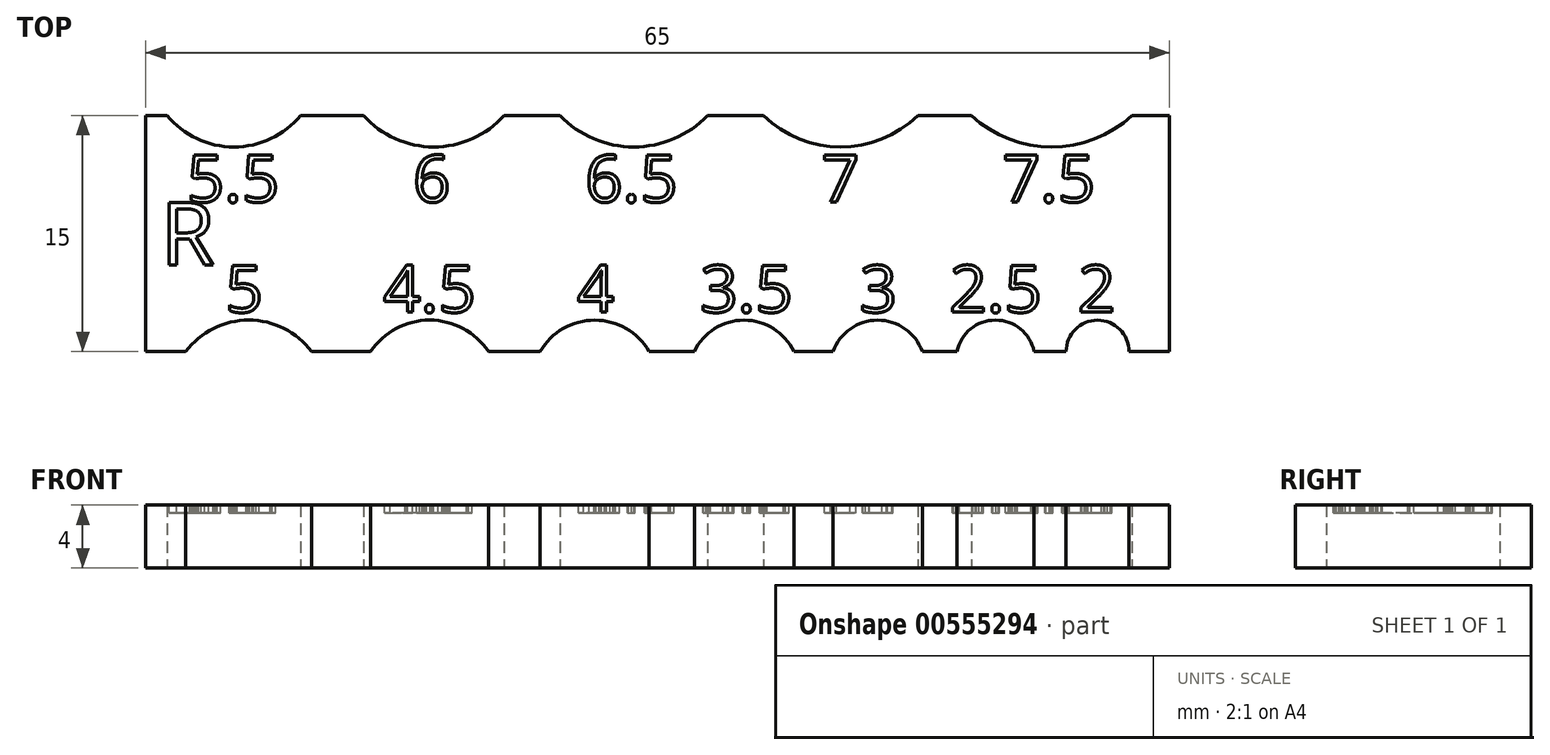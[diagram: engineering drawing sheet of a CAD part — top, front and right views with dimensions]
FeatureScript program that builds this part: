
annotation { "Feature Type Name" : "Feature", "Feature Type Description" : "" }
export const myFeature = defineFeature(function(context is Context, id is Id, definition is map)
    precondition{}
    {
        {
            var Q0;
            Q0=qCreatedBy(makeId("Top.planeOp"),FACE);
            var sketch = newSketch(context, id + "F0", { "sketchPlane" : qUnion([Q0])});
            skLineSegment(sketch, "E0", {"start": v(-84.54, 17.53) * mm, "end": v(-82, 17.53) * mm});
            skLineSegment(sketch, "E1", {"start": v(-95.27, 19.53) * mm, "end": v(54.73, 19.53) * mm, "construction": true});
            skArc(sketch, "E2", {"start": v(-74, 17.53) * mm, "mid": v(-78, 19.53) * mm, "end": v(-82, 17.53) * mm});
            skPoint(sketch, "E2.first.point", {"position": v(-74, 17.53) * mm});
            skPoint(sketch, "E2.second.point", {"position": v(-74, 17.53) * mm});
            skPoint(sketch, "E2.third.point", {"position": v(-78, 19.53) * mm});
            skArc(sketch, "E3.1.0.0", {"start": v(-62.77, 17.53) * mm, "mid": v(-66.52, 19.53) * mm, "end": v(-70.26, 17.53) * mm});
            skArc(sketch, "E3.2.0.0", {"start": v(-52.56, 17.53) * mm, "mid": v(-56.03, 19.53) * mm, "end": v(-59.5, 17.53) * mm});
            skArc(sketch, "E4.1.0.0", {"start": v(-43.38, 17.53) * mm, "mid": v(-46.54, 19.53) * mm, "end": v(-49.7, 17.53) * mm});
            skArc(sketch, "E4.2.0.0", {"start": v(-35.23, 17.53) * mm, "mid": v(-38.06, 19.53) * mm, "end": v(-40.88, 17.53) * mm});
            skArc(sketch, "E4.3.0.0", {"start": v(-28.12, 17.53) * mm, "mid": v(-30.57, 19.53) * mm, "end": v(-33.02, 17.53) * mm});
            skArc(sketch, "E4.4.0.0", {"start": v(-22.1, 17.53) * mm, "mid": v(-24.1, 19.53) * mm, "end": v(-26.1, 17.53) * mm});
            skLineSegment(sketch, "E5.trimOffspring", {"start": v(-22.1, 17.53) * mm, "end": v(-19.54, 17.53) * mm});
            skLineSegment(sketch, "E6.trimOffspring", {"start": v(-28.12, 17.53) * mm, "end": v(-26.1, 17.53) * mm});
            skLineSegment(sketch, "E7.trimOffspring", {"start": v(-35.23, 17.53) * mm, "end": v(-33.02, 17.53) * mm});
            skLineSegment(sketch, "E8.trimOffspring", {"start": v(-43.38, 17.53) * mm, "end": v(-40.88, 17.53) * mm});
            skLineSegment(sketch, "E9.trimOffspring", {"start": v(-52.56, 17.53) * mm, "end": v(-49.7, 17.53) * mm});
            skLineSegment(sketch, "E10.trimOffspring", {"start": v(-62.77, 17.53) * mm, "end": v(-59.5, 17.53) * mm});
            skLineSegment(sketch, "E11.trimOffspring", {"start": v(-74, 17.53) * mm, "end": v(-70.26, 17.53) * mm});
            skLineSegment(sketch, "E12", {"start": v(-84.54, 17.53) * mm, "end": v(-84.54, 32.53) * mm});
            skLineSegment(sketch, "E13", {"start": v(-84.54, 32.53) * mm, "end": v(-83.2, 32.53) * mm});
            skLineSegment(sketch, "E14", {"start": v(-19.54, 32.53) * mm, "end": v(-19.54, 17.53) * mm});
            skLineSegment(sketch, "E15", {"start": v(-84.54, 30.53) * mm, "end": v(-14.52, 30.53) * mm, "construction": true});
            skArc(sketch, "E16", {"start": v(-83.2, 32.53) * mm, "mid": v(-78.95, 30.53) * mm, "end": v(-74.7, 32.53) * mm});
            skPoint(sketch, "E16.first.point", {"position": v(-78.95, 30.53) * mm});
            skPoint(sketch, "E16.second.point", {"position": v(-74.7, 32.53) * mm});
            skPoint(sketch, "E16.third.point", {"position": v(-83.2, 32.53) * mm});
            skArc(sketch, "E17.1.0.0", {"start": v(-70.72, 32.53) * mm, "mid": v(-66.25, 30.53) * mm, "end": v(-61.78, 32.53) * mm});
            skArc(sketch, "E17.2.0.0", {"start": v(-58.24, 32.53) * mm, "mid": v(-53.55, 30.53) * mm, "end": v(-48.86, 32.53) * mm});
            skArc(sketch, "E17.3.0.0", {"start": v(-45.3, 32.53) * mm, "mid": v(-40.41, 30.53) * mm, "end": v(-35.51, 32.53) * mm});
            skArc(sketch, "E17.4.0.0", {"start": v(-32.1, 32.53) * mm, "mid": v(-27, 30.53) * mm, "end": v(-21.9, 32.53) * mm});
            skLineSegment(sketch, "E18.trimOffspring", {"start": v(-74.7, 32.53) * mm, "end": v(-70.72, 32.53) * mm});
            skLineSegment(sketch, "E19.trimOffspring", {"start": v(-61.78, 32.53) * mm, "end": v(-58.24, 32.53) * mm});
            skLineSegment(sketch, "E20.trimOffspring", {"start": v(-48.86, 32.53) * mm, "end": v(-45.3, 32.53) * mm});
            skLineSegment(sketch, "E21.trimOffspring", {"start": v(-35.51, 32.53) * mm, "end": v(-32.1, 32.53) * mm});
            skLineSegment(sketch, "E22.trimOffspring", {"start": v(-21.9, 32.53) * mm, "end": v(-19.54, 32.53) * mm});
            skSolve(sketch);
        }
        {
            var Q0;
            Q0 = qSketchRegion(id + "F0", true);
            extrude(context, id + "F1", {"entities" : qUnion([Q0]), "depth" : 4 * mm, "offsetDistance" : 25 * mm});
        }
        {
            var Q0;
            Q0=makeQuery(id+"F1.opExtrude","CAP_FACE",FACE,{"disambiguationData":[OSD([sQuery(id+"F0.wireOp",EDGE,"E0"),sQuery(id+"F0.wireOp",EDGE,"E2"),sQuery(id+"F0.wireOp",EDGE,"E3.1.0.0"),sQuery(id+"F0.wireOp",EDGE,"E3.2.0.0"),sQuery(id+"F0.wireOp",EDGE,"E4.1.0.0"),sQuery(id+"F0.wireOp",EDGE,"E4.2.0.0"),sQuery(id+"F0.wireOp",EDGE,"E4.3.0.0"),sQuery(id+"F0.wireOp",EDGE,"E4.4.0.0"),sQuery(id+"F0.wireOp",EDGE,"E5.trimOffspring"),sQuery(id+"F0.wireOp",EDGE,"E6.trimOffspring"),sQuery(id+"F0.wireOp",EDGE,"E7.trimOffspring"),sQuery(id+"F0.wireOp",EDGE,"E8.trimOffspring"),sQuery(id+"F0.wireOp",EDGE,"E9.trimOffspring"),sQuery(id+"F0.wireOp",EDGE,"E10.trimOffspring"),sQuery(id+"F0.wireOp",EDGE,"E11.trimOffspring"),sQuery(id+"F0.wireOp",EDGE,"E12"),sQuery(id+"F0.wireOp",EDGE,"E13"),sQuery(id+"F0.wireOp",EDGE,"E14"),sQuery(id+"F0.wireOp",EDGE,"E16"),sQuery(id+"F0.wireOp",EDGE,"E17.1.0.0"),sQuery(id+"F0.wireOp",EDGE,"E17.2.0.0"),sQuery(id+"F0.wireOp",EDGE,"E17.3.0.0"),sQuery(id+"F0.wireOp",EDGE,"E17.4.0.0"),sQuery(id+"F0.wireOp",EDGE,"E18.trimOffspring"),sQuery(id+"F0.wireOp",EDGE,"E19.trimOffspring"),sQuery(id+"F0.wireOp",EDGE,"E20.trimOffspring"),sQuery(id+"F0.wireOp",EDGE,"E21.trimOffspring"),sQuery(id+"F0.wireOp",EDGE,"E22.trimOffspring")])],"isStart":false});
            var sketch = newSketch(context, id + "F2", { "sketchPlane" : qUnion([Q0])});
            skText(sketch, "E23", { "text": "2", "fontName": "OpenSans-Regular.ttf"});
            skText(sketch, "E24", { "text": "2.5", "fontName": "OpenSans-Regular.ttf"});
            skText(sketch, "E25", { "text": "3", "fontName": "OpenSans-Regular.ttf"});
            skText(sketch, "E26", { "text": "3.5", "fontName": "OpenSans-Regular.ttf"});
            skText(sketch, "E27", { "text": "4", "fontName": "OpenSans-Regular.ttf"});
            skText(sketch, "E28", { "text": "4.5", "fontName": "OpenSans-Regular.ttf"});
            skText(sketch, "E29", { "text": "5", "fontName": "OpenSans-Regular.ttf"});
            skLineSegment(sketch, "E30", {"start": v(-83.64, 23.03) * mm, "end": v(-20.6, 23.03) * mm, "construction": true});
            skLineSegment(sketch, "E31", {"start": v(-86.71, 20.03) * mm, "end": v(-17.63, 20.03) * mm, "construction": true});
            skText(sketch, "E32", { "text": "R", "fontName": "OpenSans-Regular.ttf"});
            skText(sketch, "E33", { "text": "5.5", "fontName": "OpenSans-Regular.ttf"});
            skText(sketch, "E34", { "text": "6", "fontName": "OpenSans-Regular.ttf"});
            skText(sketch, "E35", { "text": "6.5", "fontName": "OpenSans-Regular.ttf"});
            skText(sketch, "E36", { "text": "7", "fontName": "OpenSans-Regular.ttf"});
            skText(sketch, "E37", { "text": "7.5", "fontName": "OpenSans-Regular.ttf"});
            skLineSegment(sketch, "E38", {"start": v(-85.73, 30.03) * mm, "end": v(-14.04, 30.03) * mm, "construction": true});
            skLineSegment(sketch, "E39", {"start": v(-85.73, 27.03) * mm, "end": v(-13.9, 27.03) * mm, "construction": true});
            const initialGuessF2  = {"E23": [-0.02534, 0.02003, 1, 0, 0.003], "E24": [-0.0335, 0.02003, 1, 0, 0.003], "E25": [-0.03921, 0.02003, 1, 0, 0.003], "E26": [-0.04933, 0.02003, 1, 0, 0.003], "E27": [-0.05715, 0.02003, 1, 0, 0.003], "E28": [-0.06946, 0.02003, 1, 0, 0.003], "E29": [-0.07948, 0.02003, 1, 0, 0.003], "E32": [-0.0836, 0.02303, 1, 0, 0.004], "E33": [-0.08194, 0.02703, 1, 0, 0.003], "E34": [-0.06757, 0.02703, 1, 0, 0.003], "E35": [-0.05664, 0.02703, 1, 0, 0.003], "E36": [-0.04162, 0.02703, 1, 0, 0.003], "E37": [-0.03012, 0.02703, 1, 0, 0.003]};
            skSetInitialGuess(sketch, initialGuessF2);
            skSolve(sketch);
        }
        {
            var Q0;
            Q0 = qSketchRegion(id + "F2", true);
            extrude(context, id + "F3", {"entities" : qUnion([Q0]), "operationType" : NewBodyOperationType.REMOVE, "oppositeDirection" : true, "depth" : 0.5 * mm, "offsetDistance" : 25 * mm});
        }
    });
